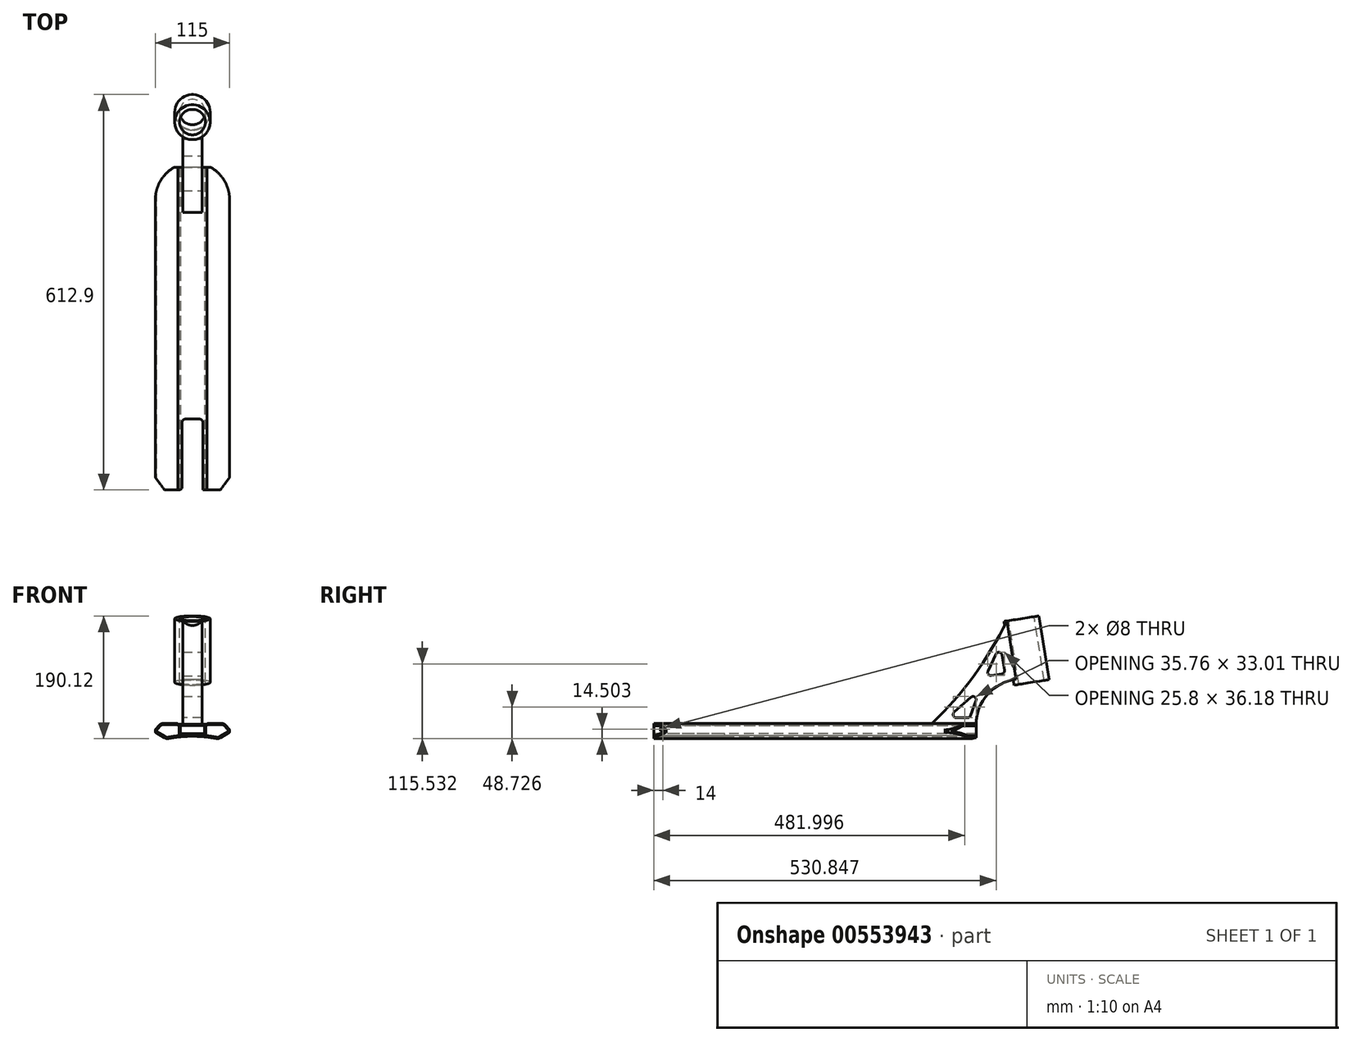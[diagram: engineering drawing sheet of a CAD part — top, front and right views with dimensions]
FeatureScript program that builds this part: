
annotation { "Feature Type Name" : "Feature", "Feature Type Description" : "" }
export const myFeature = defineFeature(function(context is Context, id is Id, definition is map)
    precondition{}
    {
        {
            var Q0;
            Q0=qCreatedBy(makeId("Front.planeOp"),FACE);
            var sketch = newSketch(context, id + "F0", { "sketchPlane" : qUnion([Q0])});
            skLineSegment(sketch, "E0", {"start": v(0, 0) * mm, "end": v(0, 13.62) * mm, "construction": true});
            skLineSegment(sketch, "E1", {"start": v(0, 0) * mm, "end": v(22.5, 0) * mm});
            skLineSegment(sketch, "E2", {"start": v(22.5, 0) * mm, "end": v(22.5, 1.3) * mm});
            skLineSegment(sketch, "E3", {"start": v(22.5, 1.3) * mm, "end": v(49.1, 1.3) * mm});
            skLineSegment(sketch, "E4", {"start": v(57.5, -8.7) * mm, "end": v(49.1, 1.3) * mm});
            skLineSegment(sketch, "E5", {"start": v(57.5, -8.7) * mm, "end": v(57.5, -12.7) * mm});
            skLineSegment(sketch, "E6", {"start": v(57.5, -12.7) * mm, "end": v(40.18, -22.7) * mm});
            skLineSegment(sketch, "E7.MirrorCS", {"start": v(0, 0) * mm, "end": v(-22.5, 0) * mm});
            skLineSegment(sketch, "E8.MirrorCS", {"start": v(-22.5, 0) * mm, "end": v(-22.5, 1.3) * mm});
            skLineSegment(sketch, "E9.MirrorCS", {"start": v(-22.5, 1.3) * mm, "end": v(-49.1, 1.3) * mm});
            skLineSegment(sketch, "E10.MirrorCS", {"start": v(-57.5, -8.7) * mm, "end": v(-49.1, 1.3) * mm});
            skLineSegment(sketch, "E11.MirrorCS", {"start": v(-57.5, -8.7) * mm, "end": v(-57.5, -12.7) * mm});
            skLineSegment(sketch, "E12.MirrorCS", {"start": v(-57.5, -12.7) * mm, "end": v(-40.18, -22.7) * mm});
            skArc(sketch, "E13", {"start": v(40.18, -22.7) * mm, "mid": v(0, -18.62) * mm, "end": v(-40.18, -22.7) * mm});
            skSolve(sketch);
        }
        {
            var Q0;
            Q0=qSketchRegion(id+"F0",true);
            extrude(context, id + "F1", {"entities" : qUnion([Q0]), "endBound" : BoundingType.SYMMETRIC, "depth" : 500 * mm});
        }
        {
            var Q0;
            Q0=qCreatedBy(makeId("Front.planeOp"),FACE);
            var sketch = newSketch(context, id + "F2", { "sketchPlane" : qUnion([Q0])});
            skLineSegment(sketch, "E14.bottom", {"start": v(19, -14.73) * mm, "end": v(-19, -14.73) * mm});
            skLineSegment(sketch, "E14.top", {"start": v(19, -1.73) * mm, "end": v(-19, -1.73) * mm});
            skLineSegment(sketch, "E14.left", {"start": v(19, -14.73) * mm, "end": v(19, -1.73) * mm});
            skLineSegment(sketch, "E14.right", {"start": v(-19, -14.73) * mm, "end": v(-19, -1.73) * mm});
            skPoint(sketch, "E14.middle", {"position": v(0, -8.23) * mm});
            skSolve(sketch);
        }
        {
            var Q0;
            Q0=qSketchRegion(id+"F2",true);
            extrude(context, id + "F3", {"entities" : qUnion([Q0]), "operationType" : NewBodyOperationType.REMOVE, "endBound" : BoundingType.SYMMETRIC, "oppositeDirection" : true, "depth" : 500 * mm});
        }
        {
            var Q0;
            Q0=makeQuery(id+"F1.opExtrude","SWEPT_EDGE",EDGE,{"disambiguationData":[OSD([sQuery(id+"F0.wireOp",EDGE,"E2"),sQuery(id+"F0.wireOp",EDGE,"E3")])]});
            var Q1;
            Q1=makeQuery(id+"F1.opExtrude","SWEPT_EDGE",EDGE,{"disambiguationData":[OSD([sQuery(id+"F0.wireOp",EDGE,"E8.MirrorCS"),sQuery(id+"F0.wireOp",EDGE,"E9.MirrorCS")])]});
            fillet(context, id + "F4", {"entities" : qUnion([Q0, Q1]), "radius" : 2 * mm, "tangentPropagation" : true, "allowEdgeOverflow" : false});
        }
        {
            var Q0;
            Q0=makeQuery(id+"F1.opExtrude","SWEPT_EDGE",EDGE,{"disambiguationData":[OSD([sQuery(id+"F0.wireOp",EDGE,"E9.MirrorCS"),sQuery(id+"F0.wireOp",EDGE,"E10.MirrorCS")])]});
            var Q1;
            Q1=makeQuery(id+"F1.opExtrude","SWEPT_EDGE",EDGE,{"disambiguationData":[OSD([sQuery(id+"F0.wireOp",EDGE,"E3"),sQuery(id+"F0.wireOp",EDGE,"E4")])]});
            var Q2;
            Q2=makeQuery(id+"F1.opExtrude","SWEPT_EDGE",EDGE,{"disambiguationData":[OSD([sQuery(id+"F0.wireOp",EDGE,"E6"),sQuery(id+"F0.wireOp",EDGE,"E13")])]});
            var Q3;
            Q3=makeQuery(id+"F1.opExtrude","SWEPT_EDGE",EDGE,{"disambiguationData":[OSD([sQuery(id+"F0.wireOp",EDGE,"E12.MirrorCS"),sQuery(id+"F0.wireOp",EDGE,"E13")])]});
            fillet(context, id + "F5", {"entities" : qUnion([Q0, Q1, Q2, Q3]), "radius" : 9 * mm, "tangentPropagation" : true, "allowEdgeOverflow" : false});
        }
        {
            var Q0;
            Q0=makeQuery(id+"F1.opExtrude","SWEPT_EDGE",EDGE,{"disambiguationData":[OSD([sQuery(id+"F0.wireOp",EDGE,"E10.MirrorCS"),sQuery(id+"F0.wireOp",EDGE,"E11.MirrorCS")])]});
            var Q1;
            Q1=makeQuery(id+"F1.opExtrude","SWEPT_EDGE",EDGE,{"disambiguationData":[OSD([sQuery(id+"F0.wireOp",EDGE,"E11.MirrorCS"),sQuery(id+"F0.wireOp",EDGE,"E12.MirrorCS")])]});
            var Q2;
            Q2=makeQuery(id+"F1.opExtrude","SWEPT_EDGE",EDGE,{"disambiguationData":[OSD([sQuery(id+"F0.wireOp",EDGE,"E4"),sQuery(id+"F0.wireOp",EDGE,"E5")])]});
            var Q3;
            Q3=makeQuery(id+"F1.opExtrude","SWEPT_EDGE",EDGE,{"disambiguationData":[OSD([sQuery(id+"F0.wireOp",EDGE,"E5"),sQuery(id+"F0.wireOp",EDGE,"E6")])]});
            fillet(context, id + "F6", {"entities" : qUnion([Q0, Q1, Q2, Q3]), "radius" : 1 * mm, "tangentPropagation" : true, "allowEdgeOverflow" : false});
        }
        {
            var Q0;
            Q0=makeQuery(id+"F1.opExtrude","CAP_FACE",FACE,{"disambiguationData":[OSD([sQuery(id+"F0.wireOp",EDGE,"E1"),sQuery(id+"F0.wireOp",EDGE,"E2"),sQuery(id+"F0.wireOp",EDGE,"E3"),sQuery(id+"F0.wireOp",EDGE,"E4"),sQuery(id+"F0.wireOp",EDGE,"E5"),sQuery(id+"F0.wireOp",EDGE,"E6"),sQuery(id+"F0.wireOp",EDGE,"E7.MirrorCS"),sQuery(id+"F0.wireOp",EDGE,"E8.MirrorCS"),sQuery(id+"F0.wireOp",EDGE,"E9.MirrorCS"),sQuery(id+"F0.wireOp",EDGE,"E10.MirrorCS"),sQuery(id+"F0.wireOp",EDGE,"E11.MirrorCS"),sQuery(id+"F0.wireOp",EDGE,"E12.MirrorCS"),sQuery(id+"F0.wireOp",EDGE,"E13")])],"isStart":false});
            var sketch = newSketch(context, id + "F7", { "sketchPlane" : qUnion([Q0])});
            skArc(sketch, "E15.0", {"start": v(-20.41, -17.66) * mm, "mid": v(-28.89, -18.7) * mm, "end": v(-37.3, -20.1) * mm});
            skArc(sketch, "E15.1", {"start": v(-42.1, -19.28) * mm, "mid": v(-39.78, -20.12) * mm, "end": v(-37.3, -20.1) * mm});
            skLineSegment(sketch, "E15.2", {"start": v(-24.37, -0.7) * mm, "end": v(-44.91, -0.7) * mm});
            skArc(sketch, "E15.3", {"start": v(-44.91, -0.7) * mm, "mid": v(-47.87, -1.36) * mm, "end": v(-50.27, -3.2) * mm});
            skLineSegment(sketch, "E15.4", {"start": v(-55.93, -9.94) * mm, "end": v(-50.27, -3.2) * mm});
            skLineSegment(sketch, "E15.5", {"start": v(-55.66, -11.45) * mm, "end": v(-42.1, -19.28) * mm});
            skPoint(sketch, "E16.visualSharp", {"position": v(-56.7, -10.85) * mm});
            skArc(sketch, "E16.filletArc", {"start": v(-55.93, -9.94) * mm, "mid": v(-56.15, -10.76) * mm, "end": v(-55.66, -11.45) * mm});
            skArc(sketch, "E17", {"start": v(-24.37, -0.7) * mm, "mid": v(-23.1, -1.15) * mm, "end": v(-22.41, -2.3) * mm});
            skLineSegment(sketch, "E18", {"start": v(-22.41, -2.3) * mm, "end": v(-20.41, -2.3) * mm});
            skLineSegment(sketch, "E19", {"start": v(-20.41, -2.3) * mm, "end": v(-20.41, -17.66) * mm});
            skLineSegment(sketch, "E20", {"start": v(0, 0) * mm, "end": v(0, 11.87) * mm, "construction": true});
            skLineSegment(sketch, "E21.MirrorCS", {"start": v(20.41, -2.3) * mm, "end": v(20.41, -17.66) * mm});
            skLineSegment(sketch, "E22.MirrorCS", {"start": v(22.41, -2.3) * mm, "end": v(20.41, -2.3) * mm});
            skArc(sketch, "E23.MirrorCS", {"start": v(24.37, -0.7) * mm, "mid": v(23.1, -1.15) * mm, "end": v(22.41, -2.3) * mm});
            skLineSegment(sketch, "E24.MirrorCS", {"start": v(24.37, -0.7) * mm, "end": v(44.91, -0.7) * mm});
            skArc(sketch, "E25.MirrorCS", {"start": v(44.91, -0.7) * mm, "mid": v(47.87, -1.36) * mm, "end": v(50.27, -3.2) * mm});
            skLineSegment(sketch, "E26.MirrorCS", {"start": v(55.93, -9.94) * mm, "end": v(50.27, -3.2) * mm});
            skArc(sketch, "E27.MirrorCS", {"start": v(55.93, -9.94) * mm, "mid": v(56.15, -10.76) * mm, "end": v(55.66, -11.45) * mm});
            skLineSegment(sketch, "E28.MirrorCS", {"start": v(55.66, -11.45) * mm, "end": v(42.1, -19.28) * mm});
            skArc(sketch, "E29.MirrorCS", {"start": v(42.1, -19.28) * mm, "mid": v(39.78, -20.12) * mm, "end": v(37.3, -20.1) * mm});
            skArc(sketch, "E30.MirrorCS", {"start": v(20.41, -17.66) * mm, "mid": v(28.89, -18.7) * mm, "end": v(37.3, -20.1) * mm});
            skSolve(sketch);
        }
        {
            var Q0;
            Q0=qSketchRegion(id+"F7",true);
            extrude(context, id + "F8", {"entities" : qUnion([Q0]), "operationType" : NewBodyOperationType.REMOVE, "endBound" : BoundingType.THROUGH_ALL, "oppositeDirection" : true, "depth" : 25 * mm});
        }
        {
            var Q0;
            Q0=qCreatedBy(makeId("Top.planeOp"),FACE);
            var sketch = newSketch(context, id + "F9", { "sketchPlane" : qUnion([Q0])});
            skArc(sketch, "E31", {"start": v(57.5, 200) * mm, "mid": v(0, 257.5) * mm, "end": v(-57.5, 200) * mm});
            skLineSegment(sketch, "E32", {"start": v(57.5, 200) * mm, "end": v(57.5, 280) * mm});
            skLineSegment(sketch, "E33", {"start": v(57.5, 280) * mm, "end": v(-57.5, 280) * mm});
            skLineSegment(sketch, "E34", {"start": v(-57.5, 280) * mm, "end": v(-57.5, 200) * mm});
            skSolve(sketch);
        }
        {
            var Q0;
            Q0=qSketchRegion(id+"F9",true);
            extrude(context, id + "F10", {"entities" : qUnion([Q0]), "operationType" : NewBodyOperationType.REMOVE, "endBound" : BoundingType.THROUGH_ALL, "oppositeDirection" : true, "depth" : 25 * mm, "hasSecondDirection" : true, "secondDirectionBound" : SecondDirectionBoundingType.THROUGH_ALL, "secondDirectionOppositeDirection" : false, "secondDirectionDepth" : 25 * mm});
        }
        {
            var Q0;
            Q0=qCreatedBy(makeId("Top.planeOp"),FACE);
            var sketch = newSketch(context, id + "F11", { "sketchPlane" : qUnion([Q0])});
            skLineSegment(sketch, "E35", {"start": v(-16, -140) * mm, "end": v(-16, -250) * mm});
            skLineSegment(sketch, "E36", {"start": v(-16, -250) * mm, "end": v(-43.3, -250) * mm});
            skLineSegment(sketch, "E37", {"start": v(-43.3, -250) * mm, "end": v(-68, -216) * mm});
            skLineSegment(sketch, "E38", {"start": v(-68, -216) * mm, "end": v(-68, -346) * mm});
            skLineSegment(sketch, "E39", {"start": v(-68, -346) * mm, "end": v(68, -346) * mm});
            skLineSegment(sketch, "E40", {"start": v(68, -346) * mm, "end": v(68, -216) * mm});
            skLineSegment(sketch, "E41", {"start": v(16, -140) * mm, "end": v(16, -250) * mm});
            skLineSegment(sketch, "E42", {"start": v(16, -250) * mm, "end": v(43.3, -250) * mm});
            skLineSegment(sketch, "E43", {"start": v(43.3, -250) * mm, "end": v(68, -216) * mm});
            skLineSegment(sketch, "E44", {"start": v(-16, -140) * mm, "end": v(16, -140) * mm});
            skSolve(sketch);
        }
        {
            var Q0;
            Q0=qSketchRegion(id+"F11",true);
            extrude(context, id + "F12", {"entities" : qUnion([Q0]), "operationType" : NewBodyOperationType.REMOVE, "endBound" : BoundingType.THROUGH_ALL, "oppositeDirection" : true, "depth" : 25 * mm, "hasSecondDirection" : true, "secondDirectionBound" : SecondDirectionBoundingType.THROUGH_ALL, "secondDirectionOppositeDirection" : false, "secondDirectionDepth" : 25 * mm});
        }
        {
            var Q0;
            {var subQ0=sQuery(id+"F11.wireOp",EDGE,"E44");var subQ1=sQuery(id+"F11.wireOp",EDGE,"E35");Q0=makeQuery(id+"F12.boolean.opBoolean","COPY",EDGE,{"disambiguationData":[TD([makeQuery(id+"F1.opExtrude","SWEPT_FACE",FACE,{"disambiguationData":[OSD([sQuery(id+"F0.wireOp",EDGE,"E13")])]})])],"derivedFrom":makeQuery(id+"F12.opExtrude","SWEPT_EDGE",EDGE,{"disambiguationData":[OSD([subQ1,subQ0])]})});}
            var Q1;
            {var subQ0=sQuery(id+"F11.wireOp",EDGE,"E35");var subQ1=sQuery(id+"F11.wireOp",EDGE,"E44");Q1=makeQuery(id+"F12.boolean.opBoolean","COPY",EDGE,{"disambiguationData":[TD([makeQuery(id+"F3.boolean.opBoolean","COPY",FACE,{"derivedFrom":makeQuery(id+"F3.opExtrude","SWEPT_FACE",FACE,{"disambiguationData":[OSD([sQuery(id+"F2.wireOp",EDGE,"E14.top")])]})})])],"derivedFrom":makeQuery(id+"F12.opExtrude","SWEPT_EDGE",EDGE,{"disambiguationData":[OSD([subQ0,subQ1])]})});}
            var Q2;
            {var subQ0=sQuery(id+"F11.wireOp",EDGE,"E41");var subQ1=sQuery(id+"F11.wireOp",EDGE,"E44");Q2=makeQuery(id+"F12.boolean.opBoolean","COPY",EDGE,{"disambiguationData":[TD([makeQuery(id+"F3.boolean.opBoolean","COPY",FACE,{"derivedFrom":makeQuery(id+"F3.opExtrude","SWEPT_FACE",FACE,{"disambiguationData":[OSD([sQuery(id+"F2.wireOp",EDGE,"E14.top")])]})})])],"derivedFrom":makeQuery(id+"F12.opExtrude","SWEPT_EDGE",EDGE,{"disambiguationData":[OSD([subQ0,subQ1])]})});}
            var Q3;
            {var subQ0=sQuery(id+"F11.wireOp",EDGE,"E44");var subQ1=sQuery(id+"F11.wireOp",EDGE,"E41");Q3=makeQuery(id+"F12.boolean.opBoolean","COPY",EDGE,{"disambiguationData":[TD([makeQuery(id+"F1.opExtrude","SWEPT_FACE",FACE,{"disambiguationData":[OSD([sQuery(id+"F0.wireOp",EDGE,"E13")])]})])],"derivedFrom":makeQuery(id+"F12.opExtrude","SWEPT_EDGE",EDGE,{"disambiguationData":[OSD([subQ1,subQ0])]})});}
            var Q4;
            {var subQ2=sQuery(id+"F11.wireOp",EDGE,"E35");Q4=makeQuery(id+"F12.boolean.opBoolean","COPY",EDGE,{"disambiguationData":[TD([makeQuery(id+"F3.boolean.opBoolean","COPY",FACE,{"derivedFrom":makeQuery(id+"F3.opExtrude","SWEPT_FACE",FACE,{"disambiguationData":[OSD([sQuery(id+"F2.wireOp",EDGE,"E14.top")])]})})])],"derivedFrom":makeQuery(id+"F12.opExtrude","SWEPT_EDGE",EDGE,{"disambiguationData":[OSD([subQ2,sQuery(id+"F11.wireOp",EDGE,"E36")])]})});}
            var Q5;
            {var subQ2=sQuery(id+"F11.wireOp",EDGE,"E41");Q5=makeQuery(id+"F12.boolean.opBoolean","COPY",EDGE,{"disambiguationData":[TD([makeQuery(id+"F3.boolean.opBoolean","COPY",FACE,{"derivedFrom":makeQuery(id+"F3.opExtrude","SWEPT_FACE",FACE,{"disambiguationData":[OSD([sQuery(id+"F2.wireOp",EDGE,"E14.top")])]})})])],"derivedFrom":makeQuery(id+"F12.opExtrude","SWEPT_EDGE",EDGE,{"disambiguationData":[OSD([subQ2,sQuery(id+"F11.wireOp",EDGE,"E42")])]})});}
            fillet(context, id + "F13", {"entities" : qUnion([Q0, Q1, Q2, Q3, Q4, Q5]), "radius" : 5 * mm, "tangentPropagation" : true, "allowEdgeOverflow" : false});
        }
        {
            var Q0;
            Q0=qCreatedBy(makeId("Right.planeOp"),FACE);
            var sketch = newSketch(context, id + "F14", { "sketchPlane" : qUnion([Q0])});
            skLineSegment(sketch, "E45", {"start": v(250, 0) * mm, "end": v(180, 0) * mm});
            skLineSegment(sketch, "E46", {"start": v(311.71, 69.5) * mm, "end": v(313.03, 61.23) * mm});
            skLineSegment(sketch, "E47", {"start": v(313.03, 61.23) * mm, "end": v(358.46, 68.43) * mm});
            skLineSegment(sketch, "E48", {"start": v(358.46, 68.43) * mm, "end": v(342.82, 167.2) * mm});
            skLineSegment(sketch, "E49", {"start": v(342.82, 167.2) * mm, "end": v(297.38, 160) * mm});
            skArc(sketch, "E50", {"start": v(180, 0) * mm, "mid": v(245.97, 74.66) * mm, "end": v(297.38, 160) * mm});
            skArc(sketch, "E51", {"start": v(311.71, 69.5) * mm, "mid": v(267.66, 46.48) * mm, "end": v(250, 0) * mm});
            skSolve(sketch);
        }
        {
            var Q0;
            Q0=qSketchRegion(id+"F14",true);
            extrude(context, id + "F15", {"entities" : qUnion([Q0]), "operationType" : NewBodyOperationType.ADD, "endBound" : BoundingType.SYMMETRIC, "depth" : 30 * mm});
        }
        {
            var Q0;
            Q0=makeQuery(id+"F15.opExtrude","SWEPT_FACE",FACE,{"disambiguationData":[OSD([sQuery(id+"F14.wireOp",EDGE,"E49")])]});
            var sketch = newSketch(context, id + "F16", { "sketchPlane" : qUnion([Q0])});
            skCircle(sketch, "E52", {"center": v(0, 341.75) * mm, "radius": 27.5 * mm});
            skSolve(sketch);
        }
        {
            var Q0;
            Q0=qSketchRegion(id+"F16",true);
            var Q1;
            Q1=makeQuery(id+"F15.opExtrude","SWEPT_FACE",FACE,{"disambiguationData":[OSD([sQuery(id+"F14.wireOp",EDGE,"E47")])]});
            extrude(context, id + "F17", {"entities" : qUnion([Q0]), "operationType" : NewBodyOperationType.ADD, "endBound" : BoundingType.UP_TO_SURFACE, "oppositeDirection" : true, "endBoundEntityFace" : qUnion([Q1]), "depth" : 25 * mm});
        }
        {
            var Q0;
            Q0=makeQuery(id+"F17.boolean.opBoolean","MERGE",FACE,{"derivedFrom":[makeQuery(id+"F15.opExtrude","SWEPT_FACE",FACE,{"disambiguationData":[OSD([sQuery(id+"F14.wireOp",EDGE,"E49")])]}),makeQuery(id+"F17.opExtrude","CAP_FACE",FACE,{"disambiguationData":[OSD([sQuery(id+"F16.wireOp",EDGE,"E52")])],"isStart":true})]});
            var sketch = newSketch(context, id + "F18", { "sketchPlane" : qUnion([Q0])});
            skPoint(sketch, "E53", {"position": v(0, 341.75) * mm});
            skSolve(sketch);
        }
        {
            var Q0;
            Q0=sQuery(id+"F18.wireOp",VERTEX,"E53");
            var Q1;
            Q1=makeQuery(id+"F1.opExtrude","SWEPT_BODY",BODY,{"disambiguationData":[OSD([sQuery(id+"F0.wireOp",EDGE,"E1"),sQuery(id+"F0.wireOp",EDGE,"E2"),sQuery(id+"F0.wireOp",EDGE,"E3"),sQuery(id+"F0.wireOp",EDGE,"E4"),sQuery(id+"F0.wireOp",EDGE,"E5"),sQuery(id+"F0.wireOp",EDGE,"E6"),sQuery(id+"F0.wireOp",EDGE,"E7.MirrorCS"),sQuery(id+"F0.wireOp",EDGE,"E8.MirrorCS"),sQuery(id+"F0.wireOp",EDGE,"E9.MirrorCS"),sQuery(id+"F0.wireOp",EDGE,"E10.MirrorCS"),sQuery(id+"F0.wireOp",EDGE,"E11.MirrorCS"),sQuery(id+"F0.wireOp",EDGE,"E12.MirrorCS"),sQuery(id+"F0.wireOp",EDGE,"E13")])]});
            hole(context, id + "F19", {"style" : HoleStyle.SIMPLE, "endStyle" : HoleEndStyle.THROUGH, "holeDiameter" : 40 * mm, "isTappedThrough" : true, "tappedDepth" : 12 * mm, "tapClearance" : 3, "locations" : qUnion([Q0]), "scope" : qUnion([Q1])});
        }
        {
            var Q0;
            Q0=makeQuery(id+"F8.boolean.opBoolean","COPY",FACE,{"derivedFrom":makeQuery(id+"F8.opExtrude","SWEPT_FACE",FACE,{"disambiguationData":[OSD([sQuery(id+"F7.wireOp",EDGE,"E21.MirrorCS")])]})});
            var sketch = newSketch(context, id + "F20", { "sketchPlane" : qUnion([Q0])});
            skPoint(sketch, "E54", {"position": v(-236, -7.72) * mm});
            skSolve(sketch);
        }
        {
            var Q0;
            Q0=sQuery(id+"F20.wireOp",VERTEX,"E54");
            var Q1;
            Q1=makeQuery(id+"F1.opExtrude","SWEPT_BODY",BODY,{"disambiguationData":[OSD([sQuery(id+"F0.wireOp",EDGE,"E1"),sQuery(id+"F0.wireOp",EDGE,"E2"),sQuery(id+"F0.wireOp",EDGE,"E3"),sQuery(id+"F0.wireOp",EDGE,"E4"),sQuery(id+"F0.wireOp",EDGE,"E5"),sQuery(id+"F0.wireOp",EDGE,"E6"),sQuery(id+"F0.wireOp",EDGE,"E7.MirrorCS"),sQuery(id+"F0.wireOp",EDGE,"E8.MirrorCS"),sQuery(id+"F0.wireOp",EDGE,"E9.MirrorCS"),sQuery(id+"F0.wireOp",EDGE,"E10.MirrorCS"),sQuery(id+"F0.wireOp",EDGE,"E11.MirrorCS"),sQuery(id+"F0.wireOp",EDGE,"E12.MirrorCS"),sQuery(id+"F0.wireOp",EDGE,"E13")])]});
            hole(context, id + "F21", {"style" : HoleStyle.SIMPLE, "endStyle" : HoleEndStyle.BLIND, "holeDiameter" : 8 * mm, "holeDepth" : 50 * mm, "isTappedThrough" : true, "tappedDepth" : 12 * mm, "tapClearance" : 3, "locations" : qUnion([Q0]), "scope" : qUnion([Q1])});
        }
        {
            var Q0;
            Q0=makeQuery(id+"F15.opExtrude","CAP_FACE",FACE,{"disambiguationData":[OSD([sQuery(id+"F14.wireOp",EDGE,"E45"),sQuery(id+"F14.wireOp",EDGE,"E46"),sQuery(id+"F14.wireOp",EDGE,"E47"),sQuery(id+"F14.wireOp",EDGE,"E48"),sQuery(id+"F14.wireOp",EDGE,"E49"),sQuery(id+"F14.wireOp",EDGE,"E50"),sQuery(id+"F14.wireOp",EDGE,"E51")])],"isStart":false});
            var sketch = newSketch(context, id + "F22", { "sketchPlane" : qUnion([Q0])});
            skLineSegment(sketch, "E55", {"start": v(256.38, 55) * mm, "end": v(240, 10) * mm});
            skLineSegment(sketch, "E56", {"start": v(240, 10) * mm, "end": v(206, 10) * mm});
            skLineSegment(sketch, "E57", {"start": v(206, 10) * mm, "end": v(256.38, 55) * mm});
            skLineSegment(sketch, "E58", {"start": v(264.47, 73.8) * mm, "end": v(294.47, 78.54) * mm});
            skLineSegment(sketch, "E59", {"start": v(294.47, 78.54) * mm, "end": v(287.34, 123.54) * mm});
            skLineSegment(sketch, "E60", {"start": v(287.34, 123.54) * mm, "end": v(264.47, 73.8) * mm});
            skSolve(sketch);
        }
        {
            var Q0;
            Q0=qSketchRegion(id+"F22",true);
            extrude(context, id + "F23", {"entities" : qUnion([Q0]), "operationType" : NewBodyOperationType.REMOVE, "endBound" : BoundingType.THROUGH_ALL, "depth" : 25 * mm, "hasSecondDirection" : true, "secondDirectionBound" : SecondDirectionBoundingType.THROUGH_ALL, "secondDirectionOppositeDirection" : true, "secondDirectionDepth" : 25 * mm});
        }
        {
            var Q0;
            Q0=makeQuery(id+"F23.boolean.opBoolean","COPY",EDGE,{"derivedFrom":makeQuery(id+"F23.opExtrude","SWEPT_EDGE",EDGE,{"disambiguationData":[OSD([sQuery(id+"F22.wireOp",EDGE,"E58"),sQuery(id+"F22.wireOp",EDGE,"E59")])]})});
            var Q1;
            Q1=makeQuery(id+"F23.boolean.opBoolean","COPY",EDGE,{"derivedFrom":makeQuery(id+"F23.opExtrude","SWEPT_EDGE",EDGE,{"disambiguationData":[OSD([sQuery(id+"F22.wireOp",EDGE,"E55"),sQuery(id+"F22.wireOp",EDGE,"E56")])]})});
            var Q2;
            Q2=makeQuery(id+"F23.boolean.opBoolean","COPY",EDGE,{"derivedFrom":makeQuery(id+"F23.opExtrude","SWEPT_EDGE",EDGE,{"disambiguationData":[OSD([sQuery(id+"F22.wireOp",EDGE,"E55"),sQuery(id+"F22.wireOp",EDGE,"E57")])]})});
            var Q3;
            Q3=makeQuery(id+"F23.boolean.opBoolean","COPY",EDGE,{"derivedFrom":makeQuery(id+"F23.opExtrude","SWEPT_EDGE",EDGE,{"disambiguationData":[OSD([sQuery(id+"F22.wireOp",EDGE,"E59"),sQuery(id+"F22.wireOp",EDGE,"E60")])]})});
            var Q4;
            Q4=makeQuery(id+"F23.boolean.opBoolean","COPY",EDGE,{"derivedFrom":makeQuery(id+"F23.opExtrude","SWEPT_EDGE",EDGE,{"disambiguationData":[OSD([sQuery(id+"F22.wireOp",EDGE,"E56"),sQuery(id+"F22.wireOp",EDGE,"E57")])]})});
            var Q5;
            Q5=makeQuery(id+"F23.boolean.opBoolean","COPY",EDGE,{"derivedFrom":makeQuery(id+"F23.opExtrude","SWEPT_EDGE",EDGE,{"disambiguationData":[OSD([sQuery(id+"F22.wireOp",EDGE,"E58"),sQuery(id+"F22.wireOp",EDGE,"E60")])]})});
            fillet(context, id + "F24", {"entities" : qUnion([Q0, Q1, Q2, Q3, Q4, Q5]), "radius" : 5 * mm, "tangentPropagation" : true, "allowEdgeOverflow" : false});
        }
    });
